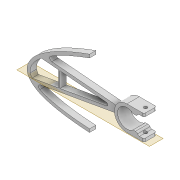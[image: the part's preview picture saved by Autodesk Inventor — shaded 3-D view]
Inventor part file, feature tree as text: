
AUTODESK INVENTOR PART (.ipt)
format: ipt  version: 2022 (Build 260153000, 153)  size: 568,832 bytes
history: native  units: mm
features: extrude x6, sketch x5, projected_geometry x3, fillet x2, shell x1
ambient origin geometry x8: Origin, YZ Plane, XZ Plane, XY Plane, X Axis, Y Axis, Z Axis, Center Point
bodies: Solid1 (feature_tree)
feature tree (17):
  extrude  "Extrusion1"  Depth=2.0mm
  shell  "Shell1"  Thickness=66.0mm
  extrude  "Extrusion9"  Depth=12.0mm
  fillet  "Fillet2"  Radius=2.0mm
  extrude  "Extrusion10"  Depth=11.0mm
  extrude  "Extrusion12"  Depth=1.745329mm
  extrude  "Extrusion15"  Depth=1.0mm
  extrude  "Extrusion16"  Depth=2.0mm
  fillet  "Fillet4"  Radius=1.0mm
  sketch  "Sketch3"  dims[d0=4.0mm d1=0.0mm d2=2.0mm d68=66.0mm]
  sketch  "Sketch25"  dims[d69=8.05mm d70=12.0mm d71=2.0mm]
  projected_geometry  "Projected Loop13"
  sketch  "Sketch26"  dims[d72=11.0mm d73=11.0mm]
  sketch  "Sketch28"  dims[d74=0.872665mm d75=1.745329mm]
  projected_geometry  "Projected Loop17"
  sketch  "Sketch33"  dims[d76=2.0mm d77=1.0mm d79=2.0mm d80=1.0mm d81=1.5mm d82=1.5mm d83=4.0mm d84=0.0mm d85=3.0mm d86=3.0mm d87=1.5mm d88=40.0mm d89=40.0mm d90=100.0mm d91=0.0mm d98=2.1mm d99=2.0mm d100=2.1mm d102=30.0mm d103=0.0mm d114=3.0mm d115=1.0mm d116=45.0mm d117=2.0mm d118=0.0mm d119=2.0mm d120=0.0mm d121=1.0mm d127=0.5mm d128=0.872665mm d129=0.5mm d130=0.872665mm]
  projected_geometry  "Projected Loop18"
